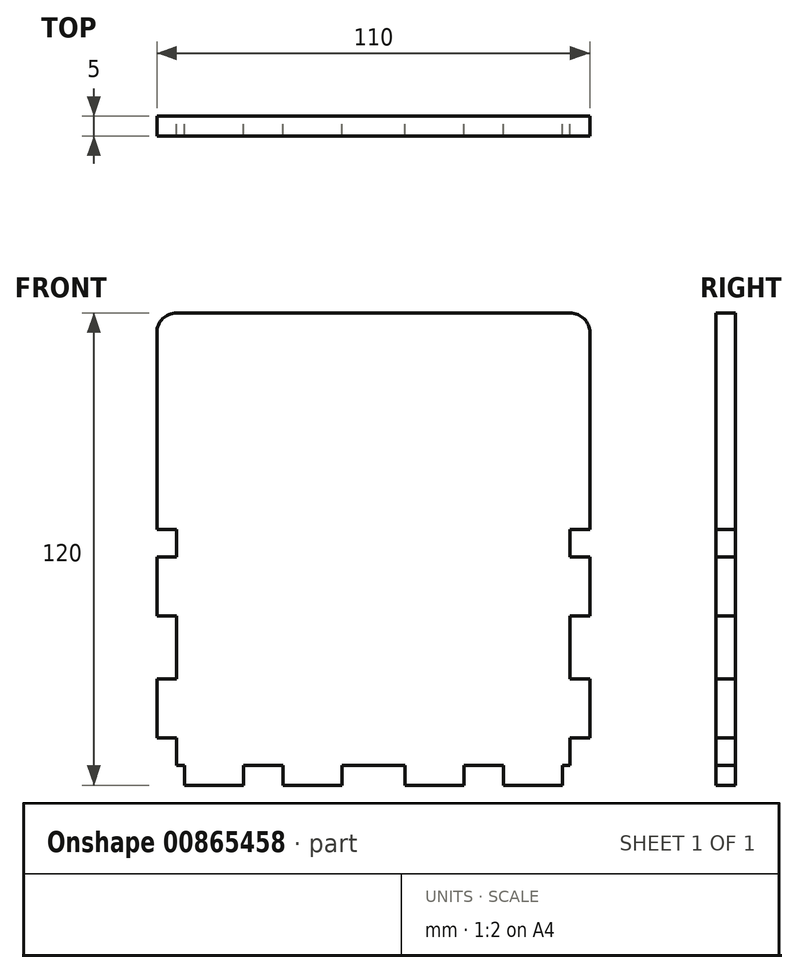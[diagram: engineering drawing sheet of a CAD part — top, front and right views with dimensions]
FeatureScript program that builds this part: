
annotation { "Feature Type Name" : "Feature", "Feature Type Description" : "" }
export const myFeature = defineFeature(function(context is Context, id is Id, definition is map)
    precondition{}
    {
        {
            var Q0;
            Q0=qCreatedBy(makeId("Front.planeOp"),FACE);
            var sketch = newSketch(context, id + "F0", { "sketchPlane" : qUnion([Q0])});
            skLineSegment(sketch, "E0.bottom", {"start": v(-100.92, 0) * mm, "end": v(-0.92, 0) * mm});
            skLineSegment(sketch, "E0.top", {"start": v(-100.92, -60) * mm, "end": v(-98.92, -60) * mm});
            skLineSegment(sketch, "E0.left", {"start": v(-100.92, 0) * mm, "end": v(-100.92, -7) * mm});
            skLineSegment(sketch, "E0.right", {"start": v(-0.92, 0) * mm, "end": v(-0.92, -7) * mm});
            skPoint(sketch, "E0.middle", {"position": v(-50.92, -30) * mm});
            skLineSegment(sketch, "E1", {"start": v(-2.92, -60) * mm, "end": v(-2.92, -65) * mm});
            skLineSegment(sketch, "E2", {"start": v(-2.92, -65) * mm, "end": v(-17.92, -65) * mm});
            skLineSegment(sketch, "E3", {"start": v(-17.92, -65) * mm, "end": v(-17.92, -60) * mm});
            skLineSegment(sketch, "E4", {"start": v(-27.92, -60) * mm, "end": v(-27.92, -65) * mm});
            skLineSegment(sketch, "E5", {"start": v(-27.92, -65) * mm, "end": v(-42.92, -65) * mm});
            skLineSegment(sketch, "E6", {"start": v(-42.92, -65) * mm, "end": v(-42.92, -60) * mm});
            skLineSegment(sketch, "E7.MirrorCS", {"start": v(-58.92, -65) * mm, "end": v(-58.92, -60) * mm});
            skLineSegment(sketch, "E8.MirrorCS", {"start": v(-73.92, -65) * mm, "end": v(-58.92, -65) * mm});
            skLineSegment(sketch, "E9.MirrorCS", {"start": v(-73.92, -60) * mm, "end": v(-73.92, -65) * mm});
            skLineSegment(sketch, "E10.MirrorCS", {"start": v(-83.92, -65) * mm, "end": v(-83.92, -60) * mm});
            skLineSegment(sketch, "E11.MirrorCS", {"start": v(-98.92, -65) * mm, "end": v(-83.92, -65) * mm});
            skLineSegment(sketch, "E12.MirrorCS", {"start": v(-98.92, -60) * mm, "end": v(-98.92, -65) * mm});
            skLineSegment(sketch, "E13.trimOffspring", {"start": v(-2.92, -60) * mm, "end": v(-0.92, -60) * mm});
            skLineSegment(sketch, "E14.trimOffspring", {"start": v(-27.92, -60) * mm, "end": v(-17.92, -60) * mm});
            skLineSegment(sketch, "E15.trimOffspring", {"start": v(-58.92, -60) * mm, "end": v(-42.92, -60) * mm});
            skLineSegment(sketch, "E16.trimOffspring", {"start": v(-83.92, -60) * mm, "end": v(-73.92, -60) * mm});
            skPoint(sketch, "E17.middle", {"position": v(-3.04, -45.5) * mm});
            skLineSegment(sketch, "E18", {"start": v(-0.92, -53) * mm, "end": v(4.08, -53) * mm});
            skLineSegment(sketch, "E19", {"start": v(4.08, -53) * mm, "end": v(4.08, -38) * mm});
            skLineSegment(sketch, "E20", {"start": v(4.08, -38) * mm, "end": v(-0.92, -38) * mm});
            skLineSegment(sketch, "E21.trimOffspring", {"start": v(-0.92, -53) * mm, "end": v(-0.92, -60) * mm});
            skLineSegment(sketch, "E22.MirrorCS", {"start": v(-100.92, -53) * mm, "end": v(-105.92, -53) * mm});
            skLineSegment(sketch, "E23.MirrorCS", {"start": v(-105.92, -53) * mm, "end": v(-105.92, -38) * mm});
            skLineSegment(sketch, "E24.MirrorCS", {"start": v(-105.92, -38) * mm, "end": v(-100.92, -38) * mm});
            skLineSegment(sketch, "E25.MirrorCS", {"start": v(4.08, -7) * mm, "end": v(4.08, -22) * mm});
            skLineSegment(sketch, "E26.MirrorCS", {"start": v(-0.92, -7) * mm, "end": v(4.08, -7) * mm});
            skLineSegment(sketch, "E27.MirrorCS", {"start": v(4.08, -22) * mm, "end": v(-0.92, -22) * mm});
            skLineSegment(sketch, "E28.MirrorCS", {"start": v(-100.92, -7) * mm, "end": v(-105.92, -7) * mm});
            skLineSegment(sketch, "E29.MirrorCS", {"start": v(-105.92, -22) * mm, "end": v(-100.92, -22) * mm});
            skLineSegment(sketch, "E30.MirrorCS", {"start": v(-105.92, -7) * mm, "end": v(-105.92, -22) * mm});
            skLineSegment(sketch, "E31.trimOffspring", {"start": v(-0.92, -22) * mm, "end": v(-0.92, -38) * mm});
            skLineSegment(sketch, "E32.trimOffspring", {"start": v(-100.92, -53) * mm, "end": v(-100.92, -60) * mm});
            skLineSegment(sketch, "E33.trimOffspring", {"start": v(-100.92, -22) * mm, "end": v(-100.92, -38) * mm});
            skLineSegment(sketch, "E34", {"start": v(-50.92, -30) * mm, "end": v(-50.92, 30) * mm});
            skLineSegment(sketch, "E35", {"start": v(-100.92, 0) * mm, "end": v(-105.92, 0) * mm});
            skLineSegment(sketch, "E36", {"start": v(-105.92, 0) * mm, "end": v(-105.92, 50) * mm});
            skLineSegment(sketch, "E37", {"start": v(-100.92, 55) * mm, "end": v(-0.92, 55) * mm});
            skLineSegment(sketch, "E38", {"start": v(4.08, 50) * mm, "end": v(4.08, 0) * mm});
            skLineSegment(sketch, "E39", {"start": v(4.08, 0) * mm, "end": v(-0.92, 0) * mm});
            skPoint(sketch, "E40.visualSharp", {"position": v(4.08, 55) * mm});
            skArc(sketch, "E40.filletArc", {"start": v(4.08, 50) * mm, "mid": v(2.61, 53.54) * mm, "end": v(-0.92, 55) * mm});
            skPoint(sketch, "E41.visualSharp", {"position": v(-105.92, 55) * mm});
            skArc(sketch, "E41.filletArc", {"start": v(-100.92, 55) * mm, "mid": v(-104.46, 53.54) * mm, "end": v(-105.92, 50) * mm});
            skSolve(sketch);
        }
        {
            var Q0;
            Q0=makeQuery(id+"F0.imprint","IMPRINT",FACE,{"disambiguationData":[TD([[makeQuery(id+"F0.imprint","IMPRINT",EDGE,{"derivedFrom":sQuery(id+"F0.wireOp",EDGE,"E0.top")}),1.0]])]});
            var Q1;
            {var subQ0=sQuery(id+"F0.wireOp",EDGE,"901f438f-cea9-4ffe-a710-1d8bee51cfb4");Q1=makeQuery(id+"F0.imprint","IMPRINT",FACE,{"disambiguationData":[TD([[makeQuery(id+"F0.imprint","IMPRINT",EDGE,{"derivedFrom":subQ0}),-1.0]])]});}
            var Q2;
            {var subQ0=sQuery(id+"F0.wireOp",EDGE,"dbad5ec9-a518-4df3-865c-111754c2e8a90.MirrorCS");Q2=makeQuery(id+"F0.imprint","IMPRINT",FACE,{"disambiguationData":[TD([[makeQuery(id+"F0.imprint","IMPRINT",EDGE,{"derivedFrom":subQ0}),1.0]])]});}
            extrude(context, id + "F1", {"entities" : qUnion([Q0, Q1, Q2]), "depth" : 5 * mm, "offsetDistance" : 25 * mm});
        }
        {
            var Q0;
            {var subQ0=sQuery(id+"F0.wireOp",EDGE,"E35");Q0=makeQuery(id+"F0.imprint","IMPRINT",FACE,{"disambiguationData":[TD([[makeQuery(id+"F0.imprint","IMPRINT",EDGE,{"derivedFrom":subQ0}),-1.0]])]});}
            extrude(context, id + "F2", {"entities" : qUnion([Q0]), "operationType" : NewBodyOperationType.ADD, "depth" : 5 * mm, "offsetDistance" : 25 * mm});
        }
        {
            var Q0;
            {var subQ0=sQuery(id+"F0.wireOp",EDGE,"E35");Q0=makeQuery(id+"F0.imprint","IMPRINT",FACE,{"disambiguationData":[TD([[makeQuery(id+"F0.imprint","IMPRINT",EDGE,{"derivedFrom":subQ0}),-1.0]])]});}
            extrude(context, id + "F3", {"entities" : qUnion([Q0]), "operationType" : NewBodyOperationType.ADD, "depth" : 5 * mm, "offsetDistance" : 25 * mm});
        }
    });
